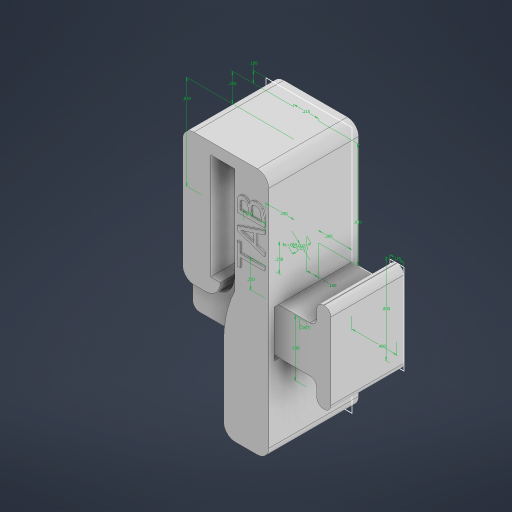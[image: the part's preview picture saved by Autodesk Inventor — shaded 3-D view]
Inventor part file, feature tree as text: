
AUTODESK INVENTOR PART (.ipt)
format: ipt  version: 2024.2 (Build 282272000, 272)  size: 390,656 bytes
history: native  units: in
note: dims shown in document units (in); Inventor stores cm internally (conversion verified against a paired STEP export)
features: extrude x6, fillet x4, thicken_offset x2, sketch x1
ambient origin geometry x8: Origin, YZ Plane, XZ Plane, XY Plane, X Axis, Y Axis, Z Axis, Center Point
bodies: Solid1 (feature_tree), Solid2 (feature_tree)
feature tree (13):
  sketch  "Sketch1"  dims[d0=0.215in d1=0.939in d2=0.027in d3=0.1in d4=0.8386in d5=0.25in d8=0.2306in d9=-0.0586in d10=0.25in d11=0.25in d12=0.1in d13=0.25in d14=0.3in d15=0.2in d16=0.4in d17=0.06in d18=0.0in d19=0.05in d20=0.0in d21=0.64in d22=0.0in d23=0.05in d24=0.0in d25=0.0669in d26=0.65in d27=0.0in d28=0.5in d29=0.01in d30=0.0in d31=0.002in d32=0.002in d33=0.002in d34=0.002in d35=1.0in d36=0.125in d37=0.8in d38=0.06in d39=0.06in d40=0.1in]
  extrude  "Extrusion1"  Depth=0.1in
  extrude  "Extrusion2"  Depth=0.1in
  extrude  "Extrusion3"  Depth=0.1in
  extrude  "Extrusion4"  Depth=0.1in
  extrude  "Extrusion5"  Depth=0.1in
  extrude  "Extrusion6"  Depth=0.1in
  thicken_offset  "Thicken1"
  thicken_offset  "Thicken2"
  fillet  "Fillet1"  [1 undecoded]
  fillet  "Fillet2"  Radius=0.25in
  fillet  "Fillet3"  Radius=0.25in
  fillet  "Fillet4"  Radius=0.1in
note: 1 required parameter value undecoded (feature->parameter linkage not recoverable at this tier; creation-order binding heuristic only, values carry confidence <= 0.55)
